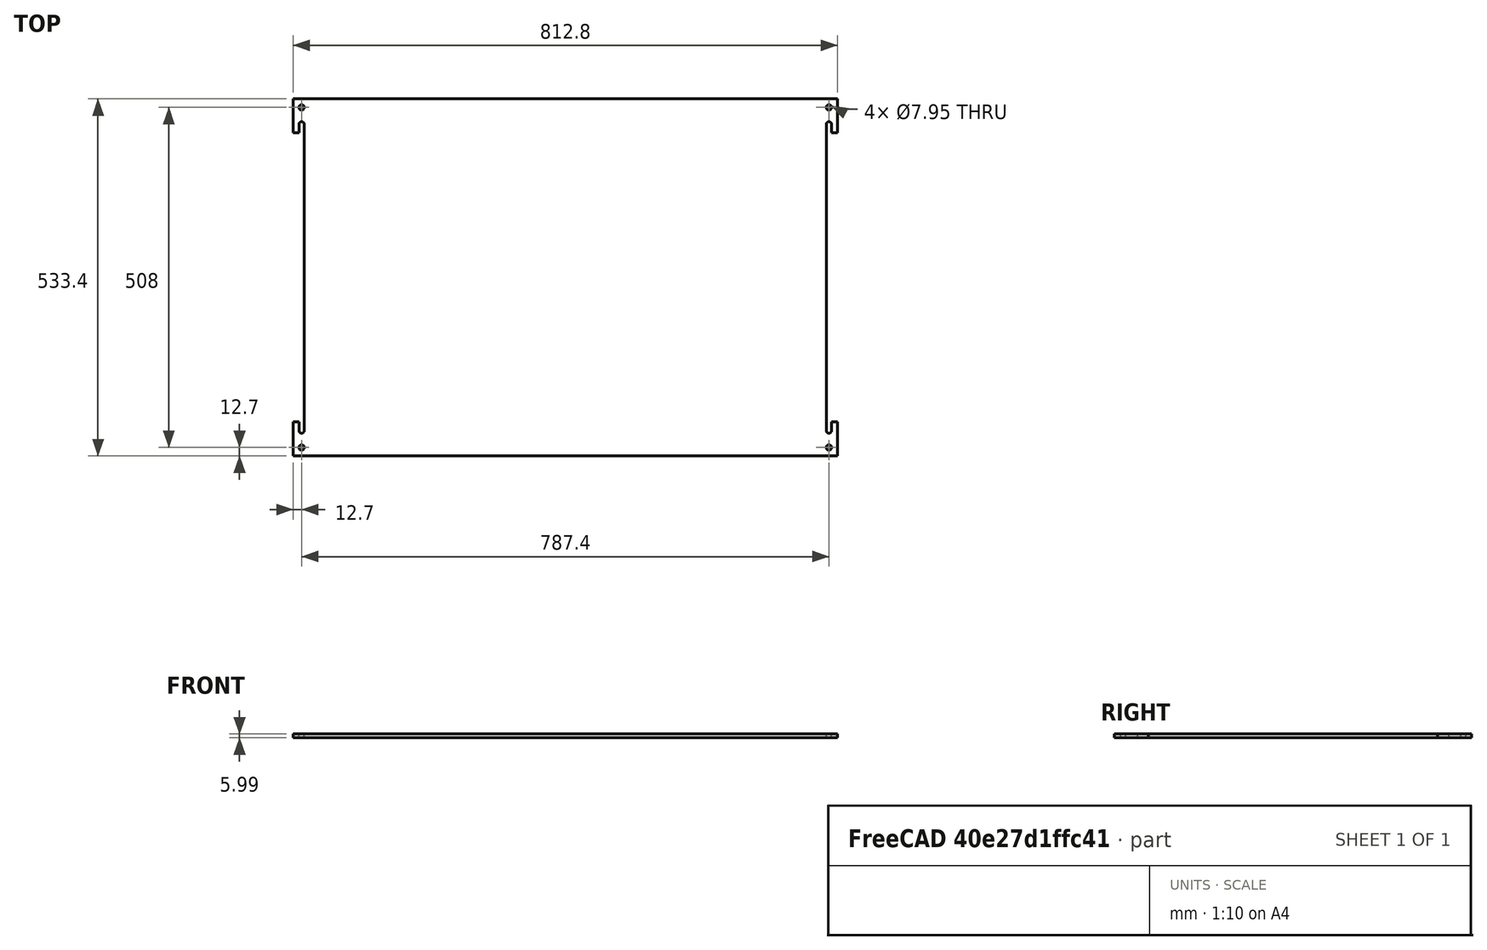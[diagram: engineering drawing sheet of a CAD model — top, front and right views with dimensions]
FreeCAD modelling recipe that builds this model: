
FCSTD DOCUMENT  (FreeCAD 0.19R24267 (Git))
Label: Inv1-P4
License: All rights reserved
LicenseURL: http://en.wikipedia.org/wiki/All_rights_reserved
objects: TechDraw::DrawViewDimension×10, TechDraw::DrawHatch×3, TechDraw::DrawViewAnnotation×3, TechDraw::DrawProjGroupItem×2, Sketcher::SketchObject×1, Part::Extrusion×1, TechDraw::DrawSVGTemplate×1, TechDraw::DrawProjGroup×1, TechDraw::DrawPage×1
note: 2 computed .brp shape members not serialized (recipe doc carries the construction recipe); baked Part::Feature solids carry a one-line shape summary decoded from their .brp

FEATURE [Sketcher::SketchObject] Sketch
  FullyConstrained = true
  sketch-geometry (40):
    g0: LineSegment StartX=0 StartY=0 StartZ=0 EndX=0 EndY=-50.8 EndZ=0
    g1: LineSegment StartX=0 StartY=-50.8 StartZ=0 EndX=8.7249 EndY=-50.8 EndZ=0
    g2: LineSegment StartX=8.7249 StartY=-50.8 StartZ=0 EndX=8.7249 EndY=-38.1 EndZ=0
    g3: LineSegment StartX=16.6751 StartY=-38.1 StartZ=0 EndX=16.6751 EndY=-495.3 EndZ=0
    g4: ArcOfCircle CenterX=12.7 CenterY=-38.1 CenterZ=0 NormalX=0 NormalY=0 NormalZ=1 AngleXU=0 Radius=3.9751 StartAngle=-1.8e-15 EndAngle=3.14159
    g5: LineSegment StartX=0 StartY=0 StartZ=0 EndX=812.8 EndY=0 EndZ=0
    g6: LineSegment StartX=8.7249 StartY=-38.1 StartZ=0 EndX=16.6751 EndY=-38.1 EndZ=0
    g7: Circle CenterX=12.7 CenterY=-12.7 CenterZ=0 NormalX=0 NormalY=0 NormalZ=1 AngleXU=0 Radius=3.9751
    g8: LineSegment StartX=812.8 StartY=0 StartZ=0 EndX=812.8 EndY=-50.8 EndZ=0
    g9: LineSegment StartX=812.8 StartY=-50.8 StartZ=0 EndX=804.075 EndY=-50.8 EndZ=0
    g10: LineSegment StartX=804.075 StartY=-50.8 StartZ=0 EndX=804.075 EndY=-38.1 EndZ=0
    g11: LineSegment StartX=796.125 StartY=-38.1 StartZ=0 EndX=796.125 EndY=-495.3 EndZ=0
    g12: LineSegment StartX=804.075 StartY=-38.1 StartZ=0 EndX=796.125 EndY=-38.1 EndZ=0
    g13: ArcOfCircle CenterX=800.1 CenterY=-38.1 CenterZ=0 NormalX=0 NormalY=0 NormalZ=1 AngleXU=0 Radius=3.9751 StartAngle=-5.95e-14 EndAngle=3.14159
    g14: Circle CenterX=800.1 CenterY=-12.7 CenterZ=0 NormalX=0 NormalY=0 NormalZ=1 AngleXU=0 Radius=3.9751
    g15: LineSegment StartX=800.1 StartY=-12.7 StartZ=0 EndX=812.8 EndY=-12.7 EndZ=0
    g16: LineSegment StartX=800.1 StartY=-12.7 StartZ=0 EndX=800.1 EndY=0 EndZ=0
    g17: LineSegment StartX=12.7 StartY=-12.7 StartZ=0 EndX=12.7 EndY=0 EndZ=0
    g18: LineSegment StartX=12.7 StartY=-12.7 StartZ=0 EndX=0 EndY=-12.7 EndZ=0
    g19: LineSegment StartX=12.7 StartY=-38.1 StartZ=0 EndX=12.7 EndY=0 EndZ=0
    g20: LineSegment StartX=800.1 StartY=0 StartZ=0 EndX=800.1 EndY=-38.1 EndZ=0
    g21: LineSegment StartX=8.7249 StartY=-495.3 StartZ=0 EndX=8.7249 EndY=-482.6 EndZ=0
    g22: LineSegment StartX=8.7249 StartY=-482.6 StartZ=0 EndX=0 EndY=-482.6 EndZ=0
    g23: LineSegment StartX=0 StartY=-482.6 StartZ=0 EndX=0 EndY=-533.4 EndZ=0
    g24: LineSegment StartX=8.7249 StartY=-495.3 StartZ=0 EndX=16.6751 EndY=-495.3 EndZ=0
    g25: ArcOfCircle CenterX=12.7 CenterY=-495.3 CenterZ=0 NormalX=0 NormalY=0 NormalZ=1 AngleXU=0 Radius=3.9751 StartAngle=3.14159 EndAngle=6.28319
    g26: Circle CenterX=12.7 CenterY=-520.7 CenterZ=0 NormalX=0 NormalY=0 NormalZ=1 AngleXU=0 Radius=3.9751
    g27: LineSegment StartX=0 StartY=-533.4 StartZ=0 EndX=812.8 EndY=-533.4 EndZ=0
    g28: LineSegment StartX=12.7 StartY=-520.7 StartZ=0 EndX=0 EndY=-520.7 EndZ=0
    g29: LineSegment StartX=12.7 StartY=-520.7 StartZ=0 EndX=12.7 EndY=-533.4 EndZ=0
    g30: LineSegment StartX=12.7 StartY=-495.3 StartZ=0 EndX=12.7 EndY=-533.4 EndZ=0
    g31: LineSegment StartX=812.8 StartY=-533.4 StartZ=0 EndX=812.8 EndY=-482.6 EndZ=0
    g32: LineSegment StartX=812.8 StartY=-482.6 StartZ=0 EndX=804.075 EndY=-482.6 EndZ=0
    g33: LineSegment StartX=804.075 StartY=-482.6 StartZ=0 EndX=804.075 EndY=-495.3 EndZ=0
    g34: LineSegment StartX=796.125 StartY=-495.3 StartZ=0 EndX=804.075 EndY=-495.3 EndZ=0
    g35: ArcOfCircle CenterX=800.1 CenterY=-495.3 CenterZ=0 NormalX=0 NormalY=0 NormalZ=1 AngleXU=0 Radius=3.9751 StartAngle=3.14159 EndAngle=6.28319
    g36: Circle CenterX=800.1 CenterY=-520.7 CenterZ=0 NormalX=0 NormalY=0 NormalZ=1 AngleXU=0 Radius=3.9751
    g37: LineSegment StartX=800.1 StartY=-495.3 StartZ=0 EndX=812.8 EndY=-495.3 EndZ=0
    g38: LineSegment StartX=800.1 StartY=-520.7 StartZ=0 EndX=800.1 EndY=-533.4 EndZ=0
    g39: LineSegment StartX=800.1 StartY=-533.4 StartZ=0 EndX=800.1 EndY=-495.3 EndZ=0
  constraints (115):
    c: Coincident(g0,g-1)
    c: Coincident(g1,g0)
    c: Horizontal(g1)
    c: Coincident(g2,g1)
    c: Vertical(g2)
    c: Vertical(g0)
    c: Vertical(g3)
    c: Coincident(g4,g2)
    c: Coincident(g4,g3)
    c: Coincident(g5,g0)
    c: Horizontal(g5)
    c: Distance(g0) = 50.8
    c: Coincident(g6,g2)
    c: Coincident(g6,g3)
    c: Horizontal(g6)
    c: PointOnObject(g4,g6)
    c: Diameter(g7) = 7.9502
    c: Distance(g5) = 812.8
    c: Coincident(g8,g5)
    c: Vertical(g8)
    c: Equal(g0,g8)
    c: Coincident(g9,g8)
    c: Horizontal(g9)
    c: Coincident(g10,g9)
    c: Vertical(g10)
    c: Vertical(g11)
    c: Coincident(g12,g10)
    c: Coincident(g12,g11)
    c: Horizontal(g12)
    c: PointOnObject(g13,g12)
    c: Coincident(g13,g11)
    c: Coincident(g13,g10)
    c: Equal(g14,g7)
    c: Equal(g7,g13)
    c: Equal(g4,g7)
    c: Coincident(g15,g14)
    c: PointOnObject(g15,g8)
    c: Horizontal(g15)
    c: Coincident(g16,g14)
    c: PointOnObject(g16,g5)
    c: Vertical(g16)
    c: Coincident(g17,g7)
    c: PointOnObject(g17,g5)
    c: Vertical(g17)
    c: Coincident(g18,g7)
    c: PointOnObject(g18,g0)
    c: Horizontal(g18)
    c: Distance(g17) = 12.7
    c: Distance(g18) = 12.7
    c: Coincident(g19,g4)
    c: Coincident(g19,g17)
    c: Vertical(g19)
    c: Distance(g19) = 38.1
    c: Equal(g16,g17)
    c: Equal(g18,g15)
    c: Coincident(g20,g16)
    c: Coincident(g20,g13)
    c: Vertical(g20)
    c: Equal(g20,g19)
    c: Vertical(g21)
    c: Coincident(g22,g21)
    c: Horizontal(g22)
    c: Vertical(g23)
    c: Coincident(g23,g22)
    c: Coincident(g24,g21)
    c: Coincident(g24,g3)
    c: Horizontal(g24)
    c: PointOnObject(g25,g24)
    c: Coincident(g25,g3)
    c: Coincident(g25,g21)
    c: Coincident(g27,g23)
    c: Horizontal(g27)
    c: PointOnObject(g23,g-2)
    c: Coincident(g28,g26)
    c: PointOnObject(g28,g23)
    c: Horizontal(g28)
    c: Coincident(g29,g26)
    c: PointOnObject(g29,g27)
    c: Vertical(g29)
    c: Equal(g29,g17)
    c: Equal(g28,g18)
    c: Coincident(g30,g25)
    c: Coincident(g30,g29)
    c: Equal(g30,g19)
    c: Equal(g23,g0)
    c: Distance(g23,g5) = 533.4
    c: Equal(g7,g26)
    c: Equal(g5,g27)
    c: Coincident(g31,g27)
    c: Vertical(g31)
    c: Coincident(g32,g31)
    c: Horizontal(g32)
    c: Coincident(g33,g32)
    c: Vertical(g33)
    c: Coincident(g34,g11)
    c: Coincident(g34,g33)
    c: Horizontal(g34)
    c: PointOnObject(g35,g34)
    c: Coincident(g35,g11)
    c: Coincident(g35,g33)
    c: Coincident(g37,g35)
    c: PointOnObject(g37,g31)
    c: Horizontal(g37)
    c: Coincident(g38,g36)
    c: PointOnObject(g38,g27)
    c: Vertical(g38)
    c: Coincident(g39,g38)
    c: Coincident(g39,g35)
    c: Vertical(g39)
    c: Equal(g31,g0)
    c: Equal(g37,g18)
    c: Vertical(g30)
    c: Equal(g38,g17)
    c: Equal(g19,g39)
    c: Equal(g36,g7)
FEATURE [Part::Extrusion] Extrude
  Base = -> Sketch
  Dir = (0,0,1)
  DirMode = 2
  FaceMakerClass = Part::FaceMakerBullseye
  LengthFwd = 5.9944
  LengthRev = 0
  Solid = true
  Symmetric = false
FEATURE [TechDraw::DrawSVGTemplate] Template
  Height = 215.9
  Orientation = 1
  Width = 279.4
FEATURE [TechDraw::DrawProjGroupItem] ProjItem  label="Front"
  CoarseView = false
  Direction = (0,0,1)
  Focus = 100
  HardHidden = false
  IsoCount = 0
  IsoHidden = false
  IsoVisible = false
  LockPosition = true
  Perspective = false
  Rotation = 0
  RotationVector = (0,1,0)
  Scale = 0.25
  ScaleType = 2
  SeamHidden = false
  SeamVisible = true
  SmoothHidden = false
  SmoothVisible = true
  Source = -> [Extrude]
  Type = 0
  X = 0
  XDirection = (1,1e-16,0)
  Y = 0
FEATURE [TechDraw::DrawProjGroupItem] ProjItem001  label="Left"
  CoarseView = false
  Direction = (-1,-1e-16,1e-16)
  Focus = 100
  HardHidden = false
  IsoCount = 0
  IsoHidden = false
  IsoVisible = false
  LockPosition = false
  Perspective = false
  Rotation = 0
  RotationVector = (1,0,0)
  Scale = 0.25
  ScaleType = 2
  SeamHidden = false
  SeamVisible = true
  SmoothHidden = false
  SmoothVisible = true
  Source = -> [Extrude]
  Type = 1
  X = 123.738
  XDirection = (1e-16,0,1)
  Y = 0
FEATURE [TechDraw::DrawProjGroup] ProjGroup
  Anchor = -> ProjItem
  AutoDistribute = true
  LockPosition = false
  ProjectionType = 0
  Rotation = 0
  Scale = 0.25
  ScaleType = 2
  Source = -> [Extrude]
  Views = -> [ProjItem,ProjItem001]
  X = 132.77
  Y = 92.7611
  spacingX = 15.0114
  spacingY = 15.0114
FEATURE [TechDraw::DrawHatch] Hatch  label="HatchF0"
  HatchPattern = <path>
  Source = -> ProjItem [Face0]
FEATURE [TechDraw::DrawHatch] Hatch001  label="Hatch001F1"
  HatchPattern = <path>
  Source = -> ProjItem001 [Face1]
FEATURE [TechDraw::DrawHatch] Hatch002  label="Hatch002F2"
  HatchPattern = <path>
  Source = -> ProjItem001 [Face2,Face3]
FEATURE [TechDraw::DrawViewDimension] Dimension
  Arbitrary = false
  ArbitraryTolerances = false
  EqualTolerance = true
  FormatSpec = %.3f
  FormatSpecOverTolerance = %+.3f
  FormatSpecUnderTolerance = %+.3f
  Inverted = false
  LockPosition = false
  MeasureType = 1
  OverTolerance = 0
  References2D = -> [ProjItem001]
  Rotation = 0
  ScaleType = 0
  TheoreticalExact = false
  Type = 1
  UnderTolerance = 0
  X = 14.2679
  Y = 63.8009
FEATURE [TechDraw::DrawViewDimension] Dimension001
  Arbitrary = false
  ArbitraryTolerances = false
  EqualTolerance = true
  FormatSpec = %.3f
  FormatSpecOverTolerance = %+.3f
  FormatSpecUnderTolerance = %+.3f
  Inverted = false
  LockPosition = false
  MeasureType = 1
  OverTolerance = 0
  References2D = -> [ProjItem]
  Rotation = 0
  ScaleType = 0
  TheoreticalExact = false
  Type = 1
  UnderTolerance = 0
  X = -0.306502
  Y = -73.3567
FEATURE [TechDraw::DrawViewDimension] Dimension002
  Arbitrary = false
  ArbitraryTolerances = false
  EqualTolerance = true
  FormatSpec = %.3f
  FormatSpecOverTolerance = %+.3f
  FormatSpecUnderTolerance = %+.3f
  Inverted = false
  LockPosition = false
  MeasureType = 1
  OverTolerance = 0
  References2D = -> [ProjItem]
  Rotation = 0
  ScaleType = 0
  TheoreticalExact = false
  Type = 2
  UnderTolerance = 0
  X = 105.89
  Y = 5.82599
FEATURE [TechDraw::DrawViewDimension] Dimension003
  Arbitrary = false
  ArbitraryTolerances = false
  EqualTolerance = true
  FormatSpec = ⌀%.3f
  FormatSpecOverTolerance = %+.3f
  FormatSpecUnderTolerance = %+.3f
  Inverted = false
  LockPosition = false
  MeasureType = 1
  OverTolerance = 0
  References2D = -> [ProjItem]
  Rotation = 0
  ScaleType = 0
  TheoreticalExact = false
  Type = 5
  UnderTolerance = 0
  X = -84.4314
  Y = 83.3245
FEATURE [TechDraw::DrawViewDimension] Dimension004
  Arbitrary = false
  ArbitraryTolerances = false
  EqualTolerance = true
  FormatSpec = %.3f
  FormatSpecOverTolerance = %+.3f
  FormatSpecUnderTolerance = %+.3f
  Inverted = false
  LockPosition = false
  MeasureType = 1
  OverTolerance = 0
  References2D = -> [ProjItem]
  Rotation = 0
  ScaleType = 0
  TheoreticalExact = false
  Type = 2
  UnderTolerance = 0
  X = -124.53
  Y = 88.7224
FEATURE [TechDraw::DrawViewDimension] Dimension005
  Arbitrary = false
  ArbitraryTolerances = false
  EqualTolerance = true
  FormatSpec = %.3f
  FormatSpecOverTolerance = %+.3f
  FormatSpecUnderTolerance = %+.3f
  Inverted = false
  LockPosition = false
  MeasureType = 1
  OverTolerance = 0
  References2D = -> [ProjItem]
  Rotation = 0
  ScaleType = 0
  TheoreticalExact = false
  Type = 1
  UnderTolerance = 0
  X = -113.324
  Y = 33.5593
FEATURE [TechDraw::DrawViewDimension] Dimension006
  Arbitrary = false
  ArbitraryTolerances = false
  EqualTolerance = true
  FormatSpec = %.3f
  FormatSpecOverTolerance = %+.3f
  FormatSpecUnderTolerance = %+.3f
  Inverted = false
  LockPosition = false
  MeasureType = 1
  OverTolerance = 0
  References2D = -> [ProjItem]
  Rotation = 0
  ScaleType = 0
  TheoreticalExact = false
  Type = 1
  UnderTolerance = 0
  X = -115.054
  Y = 43.5099
FEATURE [TechDraw::DrawViewDimension] Dimension008
  Arbitrary = false
  ArbitraryTolerances = false
  EqualTolerance = true
  FormatSpec = %.3f
  FormatSpecOverTolerance = %+.3f
  FormatSpecUnderTolerance = %+.3f
  Inverted = false
  LockPosition = false
  MeasureType = 1
  OverTolerance = 0
  References2D = -> [ProjItem]
  Rotation = 0
  ScaleType = 0
  TheoreticalExact = false
  Type = 2
  UnderTolerance = 0
  X = -61.2765
  Y = 84.2331
FEATURE [TechDraw::DrawViewDimension] Dimension009
  Arbitrary = false
  ArbitraryTolerances = false
  EqualTolerance = true
  FormatSpec = %.3f
  FormatSpecOverTolerance = %+.3f
  FormatSpecUnderTolerance = %+.3f
  Inverted = false
  LockPosition = false
  MeasureType = 1
  OverTolerance = 0
  References2D = -> [ProjItem]
  Rotation = 0
  ScaleType = 0
  TheoreticalExact = false
  Type = 1
  UnderTolerance = 0
  X = -113.581
  Y = 87.56
FEATURE [TechDraw::DrawViewDimension] Dimension010
  Arbitrary = false
  ArbitraryTolerances = false
  EqualTolerance = true
  FormatSpec = %.3f
  FormatSpecOverTolerance = %+.3f
  FormatSpecUnderTolerance = %+.3f
  Inverted = false
  LockPosition = false
  MeasureType = 1
  OverTolerance = 0
  References2D = -> [ProjItem]
  Rotation = 0
  ScaleType = 0
  TheoreticalExact = false
  Type = 2
  UnderTolerance = 0
  X = -71.5418
  Y = 81.9778
FEATURE [TechDraw::DrawViewAnnotation] Annotation
  Font = osifont
  LineSpace = 80
  LockPosition = false
  MaxWidth = -1
  Rotation = 0
  ScaleType = 0
  Text = Same each corner
  TextSize = 5.0038
  TextStyle = 0
  X = 71.346
  Y = 124.518
FEATURE [TechDraw::DrawViewAnnotation] Annotation001
  Font = osifont
  LineSpace = 80
  LockPosition = false
  MaxWidth = -1
  Rotation = 0
  ScaleType = 0
  Text = Figure S1 (Inverted 1) | Panel 4 [top] | Quantity: 1
  TextSize = 5.0038
  TextStyle = 0
  X = 32.1547
  Y = 195.58
FEATURE [TechDraw::DrawViewAnnotation] Annotation003
  Font = osifont
  LineSpace = 80
  LockPosition = false
  MaxWidth = -1
  Rotation = 0
  ScaleType = 0
  Text = Units: Inches
  TextSize = 5.0038
  TextStyle = 0
  X = 259.08
  Y = 5.08
FEATURE [TechDraw::DrawPage] Page
  KeepUpdated = true
  NextBalloonIndex = 1
  ProjectionType = 0
  Template = -> Template
  Views = -> [ProjGroup,Dimension,Dimension001,Dimension002,Dimension003,Dimension004,Dimension005,Dimension006,Dimension008,Dimension009,Dimension010,Annotation,Annotation001,Annotation003]
note: 3 file-system paths scrubbed to <path> (originals preserved in the JSON sidecar)
